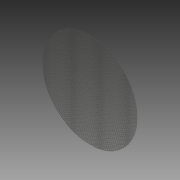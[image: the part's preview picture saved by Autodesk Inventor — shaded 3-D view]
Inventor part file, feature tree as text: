
AUTODESK INVENTOR PART (.ipt)
format: ipt  version: 2011 SP1 (Build 150282100, 282)  size: 75,776 bytes
history: native  units: in
note: dims shown in document units (in); Inventor stores cm internally (conversion verified against a paired STEP export)
features: extrude x1, sketch x1
ambient origin geometry x8: Origin, YZ Plane, XZ Plane, XY Plane, X Axis, Y Axis, Z Axis, Center Point
bodies: Solid1 (feature_tree)
feature tree (2):
  extrude  "Extrusion1"  Depth=0.0156in TaperAngle=0.0deg
  sketch  "Sketch1"  dims[d0=8.125in d1=0.0156in d2=0.0in]
